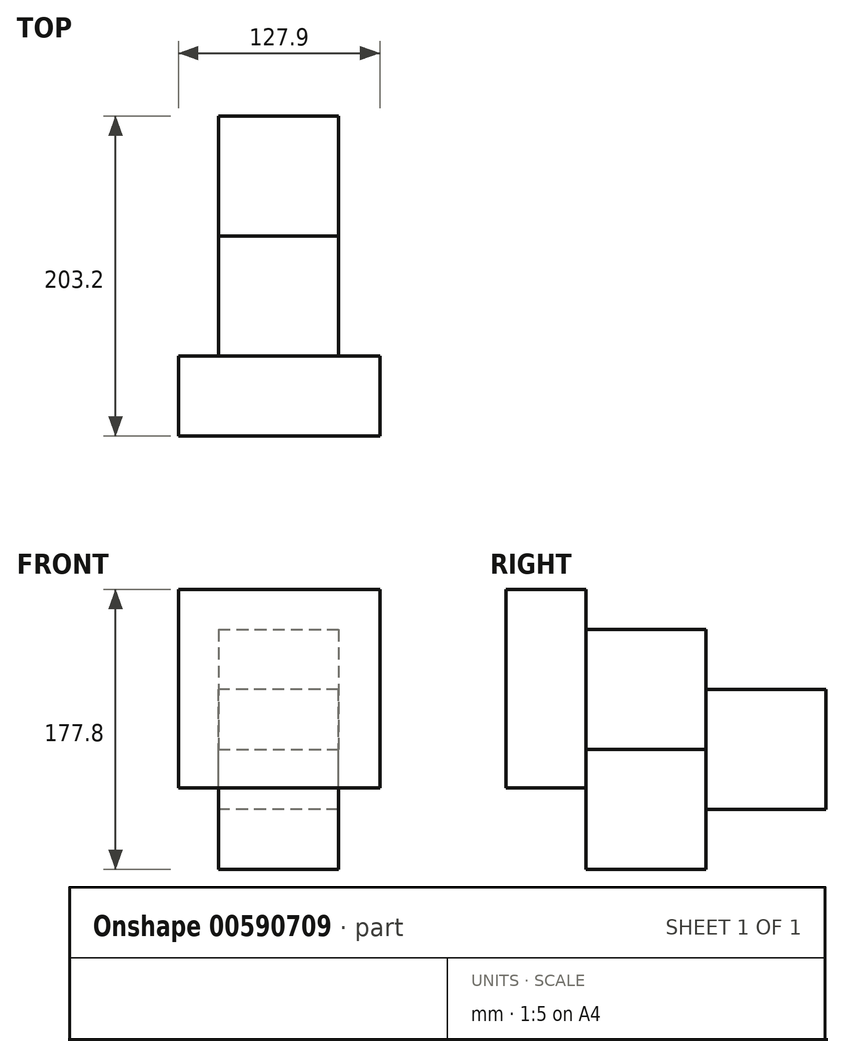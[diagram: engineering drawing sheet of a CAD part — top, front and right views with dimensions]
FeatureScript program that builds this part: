
annotation { "Feature Type Name" : "Feature", "Feature Type Description" : "" }
export const myFeature = defineFeature(function(context is Context, id is Id, definition is map)
    precondition{}
    {
        {
            var Q0;
            Q0=qCreatedBy(makeId("Top.planeOp"),FACE);
            var sketch = newSketch(context, id + "F0", { "sketchPlane" : qUnion([Q0])});
            skLineSegment(sketch, "E0.bottom", {"start": v(0, 0) * mm, "end": v(76.2, 0) * mm});
            skLineSegment(sketch, "E0.top", {"start": v(0, 76.2) * mm, "end": v(76.2, 76.2) * mm});
            skLineSegment(sketch, "E0.left", {"start": v(0, 0) * mm, "end": v(0, 76.2) * mm});
            skLineSegment(sketch, "E0.right", {"start": v(76.2, 0) * mm, "end": v(76.2, 76.2) * mm});
            skSolve(sketch);
        }
        {
            var Q0;
            Q0=makeQuery(id+"F0.imprint","IMPRINT",FACE,{"disambiguationData":[TD([[makeQuery(id+"F0.imprint","IMPRINT",EDGE,{"derivedFrom":sQuery(id+"F0.wireOp",EDGE,"E0.bottom")}),1.0]])]});
            extrude(context, id + "F1", {"entities" : qUnion([Q0]), "depth" : 76.2 * mm, "offsetDistance" : 25.4 * mm});
        }
        {
            var Q0;
            Q0=makeQuery(id+"F1.opExtrude","SWEPT_FACE",FACE,{"disambiguationData":[OSD([sQuery(id+"F0.wireOp",EDGE,"E0.bottom")])]});
            var sketch = newSketch(context, id + "F2", { "sketchPlane" : qUnion([Q0])});
            skLineSegment(sketch, "E1.bottom", {"start": v(50.8, 50.8) * mm, "end": v(25.4, 50.8) * mm});
            skLineSegment(sketch, "E1.top", {"start": v(50.8, 25.4) * mm, "end": v(25.4, 25.4) * mm});
            skLineSegment(sketch, "E1.left", {"start": v(50.8, 50.8) * mm, "end": v(50.8, 25.4) * mm});
            skLineSegment(sketch, "E1.right", {"start": v(25.4, 50.8) * mm, "end": v(25.4, 25.4) * mm});
            skPoint(sketch, "E1.middle", {"position": v(38.1, 38.1) * mm});
            skSolve(sketch);
        }
        {
            var Q0;
            Q0=makeQuery(id+"F2.imprint","IMPRINT",FACE,{"disambiguationData":[TD([[makeQuery(id+"F2.imprint","IMPRINT",EDGE,{"derivedFrom":sQuery(id+"F2.wireOp",EDGE,"E1.bottom")}),1.0]])]});
            extrude(context, id + "F3", {"entities" : qUnion([Q0]), "operationType" : NewBodyOperationType.ADD, "depth" : 25.4 * mm, "offsetDistance" : 25.4 * mm});
        }
        {
            var Q0;
            Q0=makeQuery(id+"F1.opExtrude","SWEPT_FACE",FACE,{"disambiguationData":[OSD([sQuery(id+"F0.wireOp",EDGE,"E0.bottom")])]});
            var sketch = newSketch(context, id + "F4", { "sketchPlane" : qUnion([Q0])});
            skLineSegment(sketch, "E2", {"start": v(25.4, 50.8) * mm, "end": v(50.8, 50.8) * mm});
            skLineSegment(sketch, "E3", {"start": v(50.8, 50.8) * mm, "end": v(50.8, 25.4) * mm});
            skLineSegment(sketch, "E4", {"start": v(50.8, 25.4) * mm, "end": v(25.4, 25.4) * mm});
            skLineSegment(sketch, "E5", {"start": v(25.4, 25.4) * mm, "end": v(25.4, 50.8) * mm});
            skLineSegment(sketch, "E6", {"start": v(-25.4, 101.6) * mm, "end": v(-25.4, -24.46) * mm});
            skLineSegment(sketch, "E7", {"start": v(-25.4, -24.46) * mm, "end": v(102.5, -24.46) * mm});
            skLineSegment(sketch, "E8", {"start": v(102.5, -24.46) * mm, "end": v(102.5, 101.6) * mm});
            skLineSegment(sketch, "E9", {"start": v(102.5, 101.6) * mm, "end": v(-25.4, 101.6) * mm});
            skSolve(sketch);
        }
        {
            var Q0;
            Q0=makeQuery(id+"F4.imprint","IMPRINT",FACE,{"disambiguationData":[TD([[makeQuery(id+"F4.imprint","IMPRINT",EDGE,{"derivedFrom":sQuery(id+"F4.wireOp",EDGE,"E6")}),1.0]])]});
            var Q1;
            Q1=makeQuery(id+"F4.imprint","IMPRINT",FACE,{"disambiguationData":[TD([[makeQuery(id+"F4.imprint","IMPRINT",EDGE,{"derivedFrom":sQuery(id+"F4.wireOp",EDGE,"E2")}),-1.0]])]});
            extrude(context, id + "F5", {"entities" : qUnion([Q0, Q1]), "depth" : 50.8 * mm, "offsetDistance" : 25.4 * mm});
        }
        {
            var Q0;
            Q0=makeQuery(id+"F5.opExtrude","SWEPT_FACE",FACE,{"disambiguationData":[OSD([sQuery(id+"F4.wireOp",EDGE,"E5")])]});
            var sketch = newSketch(context, id + "F6", { "sketchPlane" : qUnion([Q0])});
            skLineSegment(sketch, "E10", {"start": v(-25.4, 25.4) * mm, "end": v(-50.8, 25.4) * mm});
            skLineSegment(sketch, "E11", {"start": v(-50.8, 25.4) * mm, "end": v(-50.8, 50.8) * mm});
            skLineSegment(sketch, "E12", {"start": v(-50.8, 50.8) * mm, "end": v(-25.4, 50.8) * mm});
            skLineSegment(sketch, "E13", {"start": v(-25.4, 50.8) * mm, "end": v(-25.4, 25.4) * mm});
            skSolve(sketch);
        }
        {
            var Q0;
            Q0=makeQuery(id+"F6.imprint","IMPRINT",FACE,{"disambiguationData":[TD([[makeQuery(id+"F6.imprint","IMPRINT",EDGE,{"derivedFrom":sQuery(id+"F6.wireOp",EDGE,"E10")}),1.0]])]});
            extrude(context, id + "F7", {"entities" : qUnion([Q0]), "operationType" : NewBodyOperationType.ADD, "depth" : 25.4 * mm, "offsetDistance" : 25.4 * mm});
        }
        {
            var Q0;
            Q0=makeQuery(id+"F1.opExtrude","CAP_FACE",FACE,{"disambiguationData":[OSD([sQuery(id+"F0.wireOp",EDGE,"E0.bottom"),sQuery(id+"F0.wireOp",EDGE,"E0.top"),sQuery(id+"F0.wireOp",EDGE,"E0.left"),sQuery(id+"F0.wireOp",EDGE,"E0.right")])],"isStart":true});
            extrude(context, id + "F8", {"entities" : qUnion([Q0]), "depth" : 76.2 * mm, "offsetDistance" : 25.4 * mm});
        }
        {
            var Q0;
            Q0=makeQuery(id+"F8.opExtrude","SWEPT_FACE",FACE,{"disambiguationData":[OSD([sQuery(id+"F0.wireOp",EDGE,"E0.top")])]});
            var sketch = newSketch(context, id + "F9", { "sketchPlane" : qUnion([Q0])});
            skLineSegment(sketch, "E14.bottom", {"start": v(-76.2, -38.1) * mm, "end": v(0, -38.1) * mm});
            skLineSegment(sketch, "E14.top", {"start": v(-76.2, 38.1) * mm, "end": v(0, 38.1) * mm});
            skLineSegment(sketch, "E14.left", {"start": v(-76.2, -38.1) * mm, "end": v(-76.2, 38.1) * mm});
            skLineSegment(sketch, "E14.right", {"start": v(0, -38.1) * mm, "end": v(0, 38.1) * mm});
            skPoint(sketch, "E14.middle", {"position": v(-38.1, 0) * mm});
            skSolve(sketch);
        }
        {
            var Q0;
            {var subQ0=sQuery(id+"F9.wireOp",EDGE,"E14.bottom");Q0=makeQuery(id+"F9.imprint","IMPRINT",FACE,{"disambiguationData":[TD([[makeQuery(id+"F9.imprint","IMPRINT",EDGE,{"derivedFrom":subQ0}),1.0]])]});}
            var Q1;
            {var subQ0=sQuery(id+"F9.wireOp",EDGE,"E14.top");Q1=makeQuery(id+"F9.imprint","IMPRINT",FACE,{"disambiguationData":[TD([[makeQuery(id+"F9.imprint","IMPRINT",EDGE,{"derivedFrom":subQ0}),-1.0]])]});}
            extrude(context, id + "F10", {"entities" : qUnion([Q0, Q1]), "depth" : 76.2 * mm, "offsetDistance" : 25.4 * mm});
        }
    });
